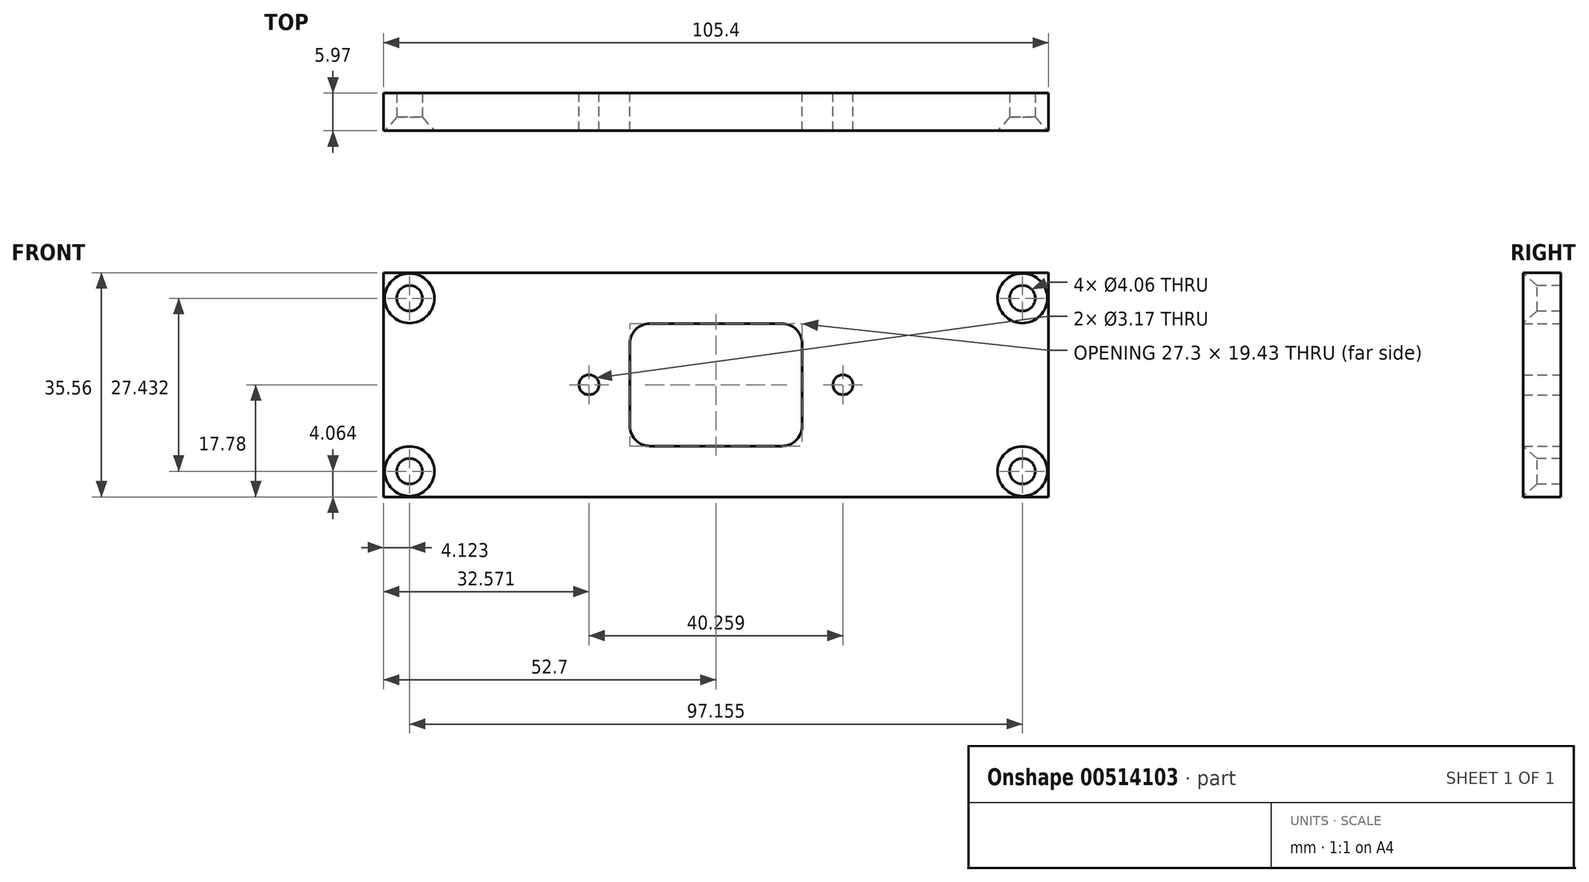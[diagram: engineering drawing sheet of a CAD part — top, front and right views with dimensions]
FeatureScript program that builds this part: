
annotation { "Feature Type Name" : "Feature", "Feature Type Description" : "" }
export const myFeature = defineFeature(function(context is Context, id is Id, definition is map)
    precondition{}
    {
        {
            var Q0;
            Q0=qCreatedBy(makeId("Front.planeOp"),FACE);
            var sketch = newSketch(context, id + "F0", { "sketchPlane" : qUnion([Q0])});
            skLineSegment(sketch, "E0.bottom", {"start": v(52.7, 17.78) * mm, "end": v(-52.7, 17.78) * mm});
            skLineSegment(sketch, "E0.top", {"start": v(52.7, -17.78) * mm, "end": v(-52.7, -17.78) * mm});
            skLineSegment(sketch, "E0.left", {"start": v(52.7, 17.78) * mm, "end": v(52.7, -17.78) * mm});
            skLineSegment(sketch, "E0.right", {"start": v(-52.7, 17.78) * mm, "end": v(-52.7, -17.78) * mm});
            skPoint(sketch, "E0.middle", {"position": v(0, 0) * mm});
            skLineSegment(sketch, "E1.bottom", {"start": v(10.48, 9.72) * mm, "end": v(-10.48, 9.72) * mm});
            skLineSegment(sketch, "E1.top", {"start": v(10.48, -9.72) * mm, "end": v(-10.48, -9.72) * mm});
            skLineSegment(sketch, "E1.left", {"start": v(13.65, 6.54) * mm, "end": v(13.65, -6.54) * mm});
            skLineSegment(sketch, "E1.right", {"start": v(-13.65, 6.54) * mm, "end": v(-13.65, -6.54) * mm});
            skPoint(sketch, "E2.visualSharp", {"position": v(13.65, 9.72) * mm});
            skArc(sketch, "E2.filletArc", {"start": v(13.65, 6.54) * mm, "mid": v(12.72, 8.79) * mm, "end": v(10.48, 9.72) * mm});
            skPoint(sketch, "E3.visualSharp", {"position": v(-13.65, 9.72) * mm});
            skArc(sketch, "E3.filletArc", {"start": v(-10.48, 9.72) * mm, "mid": v(-12.72, 8.79) * mm, "end": v(-13.65, 6.54) * mm});
            skPoint(sketch, "E4.visualSharp", {"position": v(-13.65, -9.72) * mm});
            skArc(sketch, "E4.filletArc", {"start": v(-13.65, -6.54) * mm, "mid": v(-12.72, -8.79) * mm, "end": v(-10.48, -9.72) * mm});
            skPoint(sketch, "E5.visualSharp", {"position": v(13.65, -9.72) * mm});
            skArc(sketch, "E5.filletArc", {"start": v(10.48, -9.72) * mm, "mid": v(12.72, -8.79) * mm, "end": v(13.65, -6.54) * mm});
            skCircle(sketch, "E6", {"center": v(-20.13, 0) * mm, "radius": 1.59 * mm});
            skCircle(sketch, "E7.MirrorC", {"center": v(20.13, 0) * mm, "radius": 1.59 * mm});
            skSolve(sketch);
        }
        {
            var Q0;
            Q0 = qSketchRegion(id + "F0", true);
            extrude(context, id + "F1", {"entities" : qUnion([Q0]), "depth" : 5.97 * mm, "offsetDistance" : 25.4 * mm});
        }
        {
            var Q0;
            Q0=makeQuery(id+"F1.opExtrude","CAP_FACE",FACE,{"disambiguationData":[OSD([sQuery(id+"F0.wireOp",EDGE,"E0.bottom"),sQuery(id+"F0.wireOp",EDGE,"E0.top"),sQuery(id+"F0.wireOp",EDGE,"E0.left"),sQuery(id+"F0.wireOp",EDGE,"E0.right"),sQuery(id+"F0.wireOp",EDGE,"E1.bottom"),sQuery(id+"F0.wireOp",EDGE,"E1.top"),sQuery(id+"F0.wireOp",EDGE,"E1.left"),sQuery(id+"F0.wireOp",EDGE,"E1.right"),sQuery(id+"F0.wireOp",EDGE,"E2.filletArc"),sQuery(id+"F0.wireOp",EDGE,"E3.filletArc"),sQuery(id+"F0.wireOp",EDGE,"E4.filletArc"),sQuery(id+"F0.wireOp",EDGE,"E5.filletArc"),sQuery(id+"F0.wireOp",EDGE,"E6"),sQuery(id+"F0.wireOp",EDGE,"E7.MirrorC")])],"isStart":false});
            var sketch = newSketch(context, id + "F2", { "sketchPlane" : qUnion([Q0])});
            skLineSegment(sketch, "E8", {"start": v(0, 27.77) * mm, "end": v(0, -31.04) * mm, "construction": true});
            skLineSegment(sketch, "E9", {"start": v(-58.45, 0) * mm, "end": v(61.35, 0) * mm, "construction": true});
            skLineSegment(sketch, "E10", {"start": v(-48.58, 27.59) * mm, "end": v(-48.58, -28.32) * mm, "construction": true});
            skLineSegment(sketch, "E11", {"start": v(-59, 13.72) * mm, "end": v(58.81, 13.72) * mm, "construction": true});
            skLineSegment(sketch, "E12.MirrorCS", {"start": v(-59, -13.72) * mm, "end": v(58.81, -13.72) * mm, "construction": true});
            skLineSegment(sketch, "E13.MirrorCS", {"start": v(48.58, 27.59) * mm, "end": v(48.58, -28.32) * mm, "construction": true});
            skPoint(sketch, "E14", {"position": v(-48.58, 13.72) * mm});
            skPoint(sketch, "E15", {"position": v(-48.58, -13.72) * mm});
            skPoint(sketch, "E16", {"position": v(48.58, -13.72) * mm});
            skPoint(sketch, "E17", {"position": v(48.58, 13.72) * mm});
            skSolve(sketch);
        }
        {
            var Q0;
            Q0=sQuery(id+"F2.wireOp",VERTEX,"E14");
            var Q1;
            Q1=sQuery(id+"F2.wireOp",VERTEX,"E15");
            var Q2;
            Q2=sQuery(id+"F2.wireOp",VERTEX,"E16");
            var Q3;
            Q3=sQuery(id+"F2.wireOp",VERTEX,"E17");
            var Q4;
            Q4=makeQuery(id+"F1.opExtrude","SWEPT_BODY",BODY,{"disambiguationData":[OSD([sQuery(id+"F0.wireOp",EDGE,"E0.bottom"),sQuery(id+"F0.wireOp",EDGE,"E0.top"),sQuery(id+"F0.wireOp",EDGE,"E0.left"),sQuery(id+"F0.wireOp",EDGE,"E0.right"),sQuery(id+"F0.wireOp",EDGE,"E1.bottom"),sQuery(id+"F0.wireOp",EDGE,"E1.top"),sQuery(id+"F0.wireOp",EDGE,"E1.left"),sQuery(id+"F0.wireOp",EDGE,"E1.right"),sQuery(id+"F0.wireOp",EDGE,"E2.filletArc"),sQuery(id+"F0.wireOp",EDGE,"E3.filletArc"),sQuery(id+"F0.wireOp",EDGE,"E4.filletArc"),sQuery(id+"F0.wireOp",EDGE,"E5.filletArc"),sQuery(id+"F0.wireOp",EDGE,"E6"),sQuery(id+"F0.wireOp",EDGE,"E7.MirrorC")])]});
            hole(context, id + "F3", {"style" : HoleStyle.C_SINK, "endStyle" : HoleEndStyle.BLIND, "holeDiameter" : 4.06 * mm, "cSinkDiameter" : 7.87 * mm, "cSinkAngle" : 82 * degree, "holeDepth" : 50.8 * mm, "isTappedThrough" : true, "tappedDepth" : 12.7 * mm, "tapClearance" : 3, "locations" : qUnion([Q0, Q1, Q2, Q3]), "scope" : qUnion([Q4])});
        }
    });
